# Revit family: ASH_Andria2_V4123_BIM_GB
name_source: partatom
category: Plumbing Fixtures
units: mm (PartAtom-declared; Revit-internal decimal feet)

## family parameters
Cut with Voids When Loaded = Yes
Host = Face
OmniClass Number = 23.45.05.21.11.11
OmniClass Title = Water Operated Water Closets
Part Type = Normal
Room Calculation Point = No
Round Connector Dimension = Use Diameter
Shared = Yes

## types (1)
- V412301 - Andria 2 Squatting Wc Pan
    Accessories = www.idealspec.co.uk
    AreaUnits = millimeters
    Assembly Code = C1030200
    AssetType = Fixed
    BIMObjectName = ASH_ArmitageShanks_WCPans_AndriaSquattingPan_V4123
    BIMobject category = Toilets
    BREEAMApproved = No
    Brand = Armitage Shanks
    CWFU = 0
    CodePerformance = Vitreous china to BS 3402
    ConnectionType = Plumbing
    Cost = 0 $
    Default Elevation = 0 mm  [stored 0 ft]
    Description = Andria 2 squatting wc pan
    DurationUnit = year
    EAN code = https://8595095940130
    ECA = No
    Edition number = 1
    ExpectedLife = 30
    Features = Squatting wc pan
    Finish = White
    HWFU = 0
    IFC Classification = Sanitary Terminal
    IfcExportAs = IfcSanitaryTerminalType
    IfcExportType = TOILETPAN
    Installation instructions = https://www.idealspec.co.uk
    InstallationInstructions = www.idealspec.co.uk/resources.html
    LinearUnits = millimeters
    Manufacturer name = Armitage Shanks
    ManufacturerURL = www.idealspec.co.uk
    Model = V412301
    ModelNumber = V412301
    ModelReference = Andria 2 squatting wc pan
    NBS Reference Code = 35-93-90
    NBS Reference Description = Wc Cisterns
    Name = WCPans_Andria-squattingpan_V4123_ArmitageShanks
    NettWeight = 17 Kg
    Nominal height = 212
    Nominal width = 534
    NominalDepth = 605 mm
    NominalLength = 605 mm
    OmniClass Code = 23-31 19 19
    OmniClass Description = Water Closets??
    PanColor = White
    PanMaterial = Vitreous china
    PanMounting = Other
    Product Guid = 9c926a12-f600-4d32-a0e0-eab15434fc1c
    Product SKU = V4123
    Product data url = https://bimobject.com
    Product family = Sanitary
    Product group = WC pans
    ProductInformation = www.idealspec.co.uk/assets/datasheet/V412301
    QR code = http://bimobject.com
    Shape = Sculptured
    Size = 605 x 533 x 212 mm
    Space = Internal
    SpilloverLevel = 45 mm
    Technical description = https://www.idealspec.co.uk
    ToiletPanType = WashDown
    ToiletType = Other
    URL = www.idealspec.co.uk
    Uniclass 2.0 Code = PR-35-93-90
    Uniclass 2.0 Description = Wc Cisterns
    Uniclass 2015 Code = Pr_40_20_93_89
    Uniclass 2015 Name = WC cisterns
    Version = 1
    VolumeUnits = Litres
    WFU = 0
    WRAS = No
    WarrantyDescription = Manufacturers Warranty
    WarrantyDurationParts = 99
    WarrantyDurationUnit = year
    WaterEfficientProduct = No
    Weight Net (Kg) = 17

note: [stored X ft] marks values corroborated as IEEE doubles in the binary element streams (Revit-internal decimal feet)

## geometry (parser evidence)
native form markers: Blend x4, Sweep x1
no freeform markers — native parametric forms only
